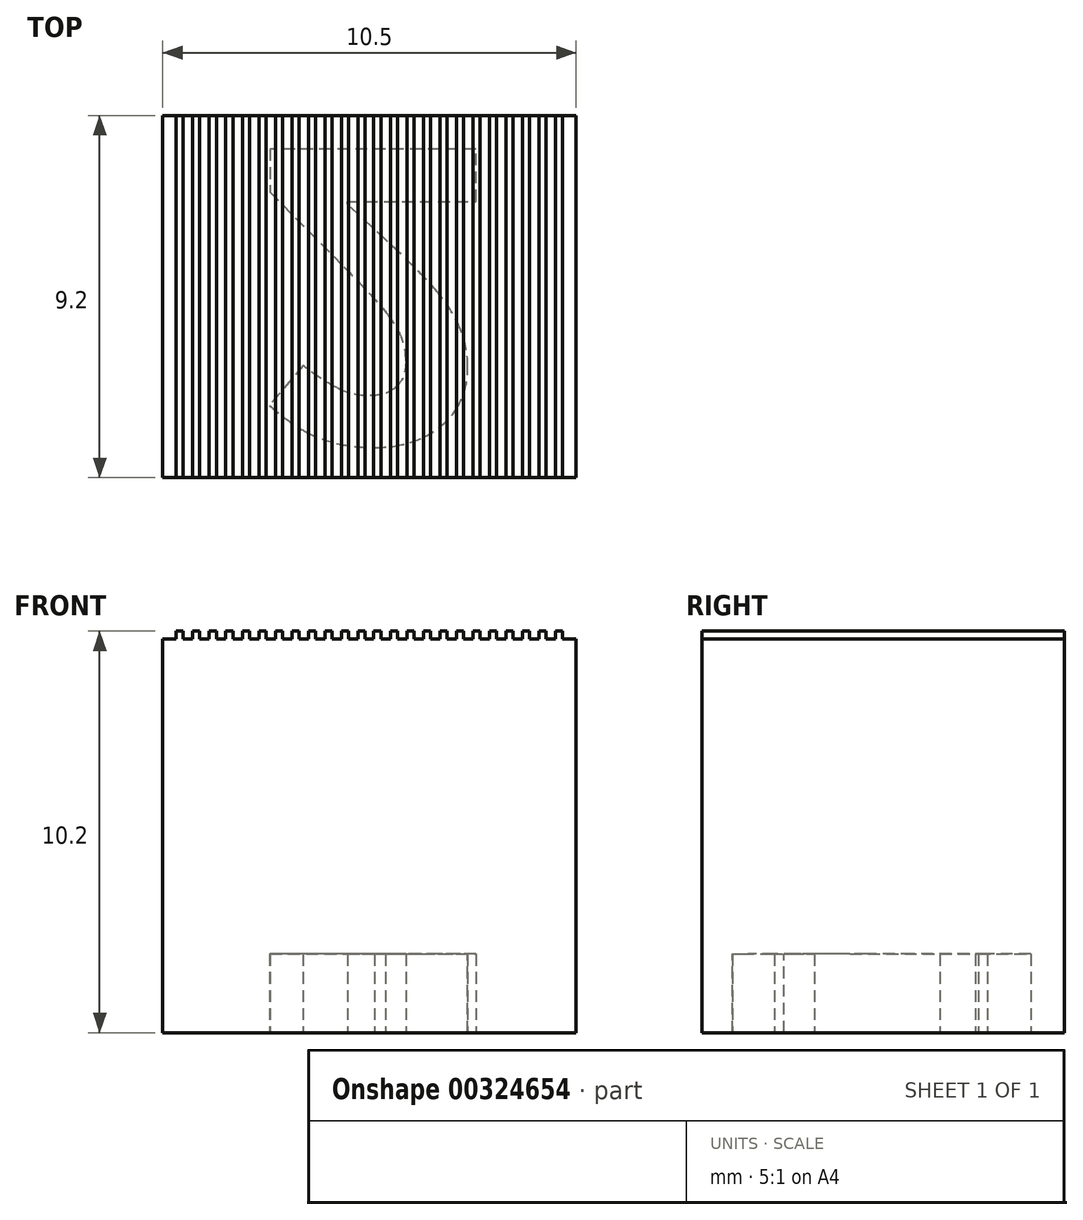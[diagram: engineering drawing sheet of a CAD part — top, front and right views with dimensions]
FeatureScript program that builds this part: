
annotation { "Feature Type Name" : "Feature", "Feature Type Description" : "" }
export const myFeature = defineFeature(function(context is Context, id is Id, definition is map)
    precondition{}
    {
        {
            assignVariable(context, id + "F0", {"name" : "h", "anyValue" : 10});
        }
        {
            assignVariable(context, id + "F1", {"name" : "gh", "anyValue" : 0.2});
        }
        {
            var Q0;
            Q0=qCreatedBy(makeId("Top.planeOp"),FACE);
            var sketch = newSketch(context, id + "F2", { "sketchPlane" : qUnion([Q0])});
            skLineSegment(sketch, "E0.bottom", {"start": v(5.25, 4.6) * mm, "end": v(-5.25, 4.6) * mm});
            skLineSegment(sketch, "E0.top", {"start": v(5.25, -4.6) * mm, "end": v(-5.25, -4.6) * mm});
            skLineSegment(sketch, "E0.left", {"start": v(5.25, 4.6) * mm, "end": v(5.25, -4.6) * mm});
            skLineSegment(sketch, "E0.right", {"start": v(-5.25, 4.6) * mm, "end": v(-5.25, -4.6) * mm});
            skPoint(sketch, "E0.middle", {"position": v(0, 0) * mm});
            skSolve(sketch);
        }
        {
            var Q0;
            Q0=qSketchRegion(id+"F2",true);
            extrude(context, id + "F3", {"entities" : qUnion([Q0]), "depth" : (getVariable(context, 'h')) * mm});
        }
        {
            var Q0;
            Q0=makeQuery(id+"F3.opExtrude","CAP_FACE",FACE,{"disambiguationData":[OSD([sQuery(id+"F2.wireOp",EDGE,"E0.bottom"),sQuery(id+"F2.wireOp",EDGE,"E0.top"),sQuery(id+"F2.wireOp",EDGE,"E0.left"),sQuery(id+"F2.wireOp",EDGE,"E0.right")])],"isStart":false});
            var sketch = newSketch(context, id + "F4", { "sketchPlane" : qUnion([Q0])});
            skLineSegment(sketch, "E1", {"start": v(0.1, 4.6) * mm, "end": v(0.11, -4.6) * mm});
            skLineSegment(sketch, "E2", {"start": v(-0.1, -4.6) * mm, "end": v(-0.11, 4.6) * mm, "construction": true});
            skLineSegment(sketch, "E3", {"start": v(0.3, -4.6) * mm, "end": v(0.29, 4.6) * mm});
            skLineSegment(sketch, "E4", {"start": v(0.1, 0) * mm, "end": v(-0.1, 0) * mm, "construction": true});
            skPoint(sketch, "E5", {"position": v(0, 0) * mm});
            skLineSegment(sketch, "E6", {"start": v(0.11, 4.6) * mm, "end": v(0.29, 4.6) * mm});
            skLineSegment(sketch, "E7", {"start": v(0.29, -4.6) * mm, "end": v(0.11, -4.6) * mm});
            skLineSegment(sketch, "E8.1.0.0", {"start": v(0.53, 4.6) * mm, "end": v(0.71, 4.6) * mm});
            skLineSegment(sketch, "E8.1.0.1", {"start": v(0.71, -4.6) * mm, "end": v(0.7, 4.6) * mm});
            skLineSegment(sketch, "E8.1.0.2", {"start": v(0.53, 4.6) * mm, "end": v(0.53, -4.6) * mm});
            skLineSegment(sketch, "E8.1.0.3", {"start": v(0.71, -4.6) * mm, "end": v(0.53, -4.6) * mm});
            skLineSegment(sketch, "E8.direction1", {"start": v(0.11, 4.6) * mm, "end": v(0.53, 4.6) * mm, "construction": true});
            skLineSegment(sketch, "E9.MirrorCS", {"start": v(-0.1, 0) * mm, "end": v(0.1, 0) * mm, "construction": true});
            skLineSegment(sketch, "E10.MirrorCS", {"start": v(-0.1, 4.6) * mm, "end": v(-0.1, -4.6) * mm});
            skLineSegment(sketch, "E11.MirrorCS", {"start": v(0.11, -4.6) * mm, "end": v(0.1, 4.6) * mm, "construction": true});
            skLineSegment(sketch, "E12.0.2.0", {"start": v(0.95, 4.6) * mm, "end": v(1.13, 4.6) * mm});
            skLineSegment(sketch, "E12.3.2.0", {"start": v(1.13, -4.6) * mm, "end": v(1.13, 4.6) * mm});
            skLineSegment(sketch, "E12.6.2.0", {"start": v(0.95, 4.6) * mm, "end": v(0.95, -4.6) * mm});
            skLineSegment(sketch, "E12.9.2.0", {"start": v(1.13, -4.6) * mm, "end": v(0.95, -4.6) * mm});
            skLineSegment(sketch, "E12.0.3.0", {"start": v(1.37, 4.6) * mm, "end": v(1.55, 4.6) * mm});
            skLineSegment(sketch, "E12.3.3.0", {"start": v(1.55, -4.6) * mm, "end": v(1.55, 4.6) * mm});
            skLineSegment(sketch, "E12.6.3.0", {"start": v(1.37, 4.6) * mm, "end": v(1.37, -4.6) * mm});
            skLineSegment(sketch, "E12.9.3.0", {"start": v(1.55, -4.6) * mm, "end": v(1.37, -4.6) * mm});
            skLineSegment(sketch, "E12.0.4.0", {"start": v(1.79, 4.6) * mm, "end": v(1.97, 4.6) * mm});
            skLineSegment(sketch, "E12.3.4.0", {"start": v(1.97, -4.6) * mm, "end": v(1.97, 4.6) * mm});
            skLineSegment(sketch, "E12.6.4.0", {"start": v(1.79, 4.6) * mm, "end": v(1.79, -4.6) * mm});
            skLineSegment(sketch, "E12.9.4.0", {"start": v(1.97, -4.6) * mm, "end": v(1.79, -4.6) * mm});
            skLineSegment(sketch, "E13.0.5.0", {"start": v(2.2, 4.6) * mm, "end": v(2.39, 4.6) * mm});
            skLineSegment(sketch, "E13.3.5.0", {"start": v(2.39, -4.6) * mm, "end": v(2.39, 4.6) * mm});
            skLineSegment(sketch, "E13.6.5.0", {"start": v(2.2, 4.6) * mm, "end": v(2.2, -4.6) * mm});
            skLineSegment(sketch, "E13.9.5.0", {"start": v(2.39, -4.6) * mm, "end": v(2.2, -4.6) * mm});
            skLineSegment(sketch, "E14.0.6.0", {"start": v(2.63, 4.6) * mm, "end": v(2.8, 4.6) * mm});
            skLineSegment(sketch, "E14.3.6.0", {"start": v(2.8, -4.6) * mm, "end": v(2.8, 4.6) * mm});
            skLineSegment(sketch, "E14.6.6.0", {"start": v(2.63, 4.6) * mm, "end": v(2.63, -4.6) * mm});
            skLineSegment(sketch, "E14.9.6.0", {"start": v(2.8, -4.6) * mm, "end": v(2.63, -4.6) * mm});
            skLineSegment(sketch, "E14.0.7.0", {"start": v(3.05, 4.6) * mm, "end": v(3.23, 4.6) * mm});
            skLineSegment(sketch, "E14.3.7.0", {"start": v(3.23, -4.6) * mm, "end": v(3.23, 4.6) * mm});
            skLineSegment(sketch, "E14.6.7.0", {"start": v(3.05, 4.6) * mm, "end": v(3.05, -4.6) * mm});
            skLineSegment(sketch, "E14.9.7.0", {"start": v(3.23, -4.6) * mm, "end": v(3.05, -4.6) * mm});
            skLineSegment(sketch, "E14.0.8.0", {"start": v(3.47, 4.6) * mm, "end": v(3.65, 4.6) * mm});
            skLineSegment(sketch, "E14.3.8.0", {"start": v(3.65, -4.6) * mm, "end": v(3.65, 4.6) * mm});
            skLineSegment(sketch, "E14.6.8.0", {"start": v(3.47, 4.6) * mm, "end": v(3.47, -4.6) * mm});
            skLineSegment(sketch, "E14.9.8.0", {"start": v(3.65, -4.6) * mm, "end": v(3.47, -4.6) * mm});
            skLineSegment(sketch, "E14.0.9.0", {"start": v(3.89, 4.6) * mm, "end": v(4.07, 4.6) * mm});
            skLineSegment(sketch, "E14.3.9.0", {"start": v(4.07, -4.6) * mm, "end": v(4.07, 4.6) * mm});
            skLineSegment(sketch, "E14.6.9.0", {"start": v(3.89, 4.6) * mm, "end": v(3.89, -4.6) * mm});
            skLineSegment(sketch, "E14.9.9.0", {"start": v(4.07, -4.6) * mm, "end": v(3.89, -4.6) * mm});
            skLineSegment(sketch, "E14.0.10.0", {"start": v(4.3, 4.6) * mm, "end": v(4.49, 4.6) * mm});
            skLineSegment(sketch, "E14.3.10.0", {"start": v(4.49, -4.6) * mm, "end": v(4.49, 4.6) * mm});
            skLineSegment(sketch, "E14.6.10.0", {"start": v(4.3, 4.6) * mm, "end": v(4.3, -4.6) * mm});
            skLineSegment(sketch, "E14.9.10.0", {"start": v(4.49, -4.6) * mm, "end": v(4.3, -4.6) * mm});
            skLineSegment(sketch, "E14.0.11.0", {"start": v(4.73, 4.6) * mm, "end": v(4.9, 4.6) * mm});
            skLineSegment(sketch, "E14.3.11.0", {"start": v(4.9, -4.6) * mm, "end": v(4.9, 4.6) * mm});
            skLineSegment(sketch, "E14.6.11.0", {"start": v(4.73, 4.6) * mm, "end": v(4.73, -4.6) * mm});
            skLineSegment(sketch, "E14.9.11.0", {"start": v(4.9, -4.6) * mm, "end": v(4.73, -4.6) * mm});
            skLineSegment(sketch, "E15.MirrorCS", {"start": v(-0.11, 4.6) * mm, "end": v(-0.29, 4.6) * mm});
            skLineSegment(sketch, "E16.MirrorCS", {"start": v(-4.73, 4.6) * mm, "end": v(-4.9, 4.6) * mm});
            skLineSegment(sketch, "E17.MirrorCS", {"start": v(-3.89, 4.6) * mm, "end": v(-4.07, 4.6) * mm});
            skLineSegment(sketch, "E18.MirrorCS", {"start": v(-4.3, 4.6) * mm, "end": v(-4.49, 4.6) * mm});
            skLineSegment(sketch, "E19.MirrorCS", {"start": v(-0.11, 4.6) * mm, "end": v(-0.53, 4.6) * mm, "construction": true});
            skLineSegment(sketch, "E20.MirrorCS", {"start": v(-2.63, 4.6) * mm, "end": v(-2.8, 4.6) * mm});
            skLineSegment(sketch, "E21.MirrorCS", {"start": v(-1.79, 4.6) * mm, "end": v(-1.97, 4.6) * mm});
            skLineSegment(sketch, "E22.MirrorCS", {"start": v(-2.2, 4.6) * mm, "end": v(-2.39, 4.6) * mm});
            skLineSegment(sketch, "E23.MirrorCS", {"start": v(-0.95, 4.6) * mm, "end": v(-1.13, 4.6) * mm});
            skLineSegment(sketch, "E24.MirrorCS", {"start": v(-3.47, 4.6) * mm, "end": v(-3.65, 4.6) * mm});
            skLineSegment(sketch, "E25.MirrorCS", {"start": v(-0.53, 4.6) * mm, "end": v(-0.71, 4.6) * mm});
            skLineSegment(sketch, "E26.MirrorCS", {"start": v(-3.05, 4.6) * mm, "end": v(-3.23, 4.6) * mm});
            skLineSegment(sketch, "E27.MirrorCS", {"start": v(-1.37, 4.6) * mm, "end": v(-1.55, 4.6) * mm});
            skLineSegment(sketch, "E28.MirrorCS", {"start": v(-0.3, -4.6) * mm, "end": v(-0.29, 4.6) * mm});
            skLineSegment(sketch, "E29.MirrorCS", {"start": v(-0.53, 4.6) * mm, "end": v(-0.53, -4.6) * mm});
            skLineSegment(sketch, "E30.MirrorCS", {"start": v(-0.71, -4.6) * mm, "end": v(-0.7, 4.6) * mm});
            skLineSegment(sketch, "E31.MirrorCS", {"start": v(-0.95, 4.6) * mm, "end": v(-0.95, -4.6) * mm});
            skLineSegment(sketch, "E32.MirrorCS", {"start": v(-1.13, -4.6) * mm, "end": v(-1.13, 4.6) * mm});
            skLineSegment(sketch, "E33.MirrorCS", {"start": v(-1.37, 4.6) * mm, "end": v(-1.37, -4.6) * mm});
            skLineSegment(sketch, "E34.MirrorCS", {"start": v(-1.55, -4.6) * mm, "end": v(-1.55, 4.6) * mm});
            skLineSegment(sketch, "E35.MirrorCS", {"start": v(-1.79, 4.6) * mm, "end": v(-1.79, -4.6) * mm});
            skLineSegment(sketch, "E36.MirrorCS", {"start": v(-1.97, -4.6) * mm, "end": v(-1.97, 4.6) * mm});
            skLineSegment(sketch, "E37.MirrorCS", {"start": v(-2.2, 4.6) * mm, "end": v(-2.2, -4.6) * mm});
            skLineSegment(sketch, "E38.MirrorCS", {"start": v(-2.39, -4.6) * mm, "end": v(-2.39, 4.6) * mm});
            skLineSegment(sketch, "E39.MirrorCS", {"start": v(-2.63, 4.6) * mm, "end": v(-2.63, -4.6) * mm});
            skLineSegment(sketch, "E40.MirrorCS", {"start": v(-2.8, -4.6) * mm, "end": v(-2.8, 4.6) * mm});
            skLineSegment(sketch, "E41.MirrorCS", {"start": v(-3.05, 4.6) * mm, "end": v(-3.05, -4.6) * mm});
            skLineSegment(sketch, "E42.MirrorCS", {"start": v(-3.23, -4.6) * mm, "end": v(-3.23, 4.6) * mm});
            skLineSegment(sketch, "E43.MirrorCS", {"start": v(-3.47, 4.6) * mm, "end": v(-3.47, -4.6) * mm});
            skLineSegment(sketch, "E44.MirrorCS", {"start": v(-3.65, -4.6) * mm, "end": v(-3.65, 4.6) * mm});
            skLineSegment(sketch, "E45.MirrorCS", {"start": v(-3.89, 4.6) * mm, "end": v(-3.89, -4.6) * mm});
            skLineSegment(sketch, "E46.MirrorCS", {"start": v(-4.07, -4.6) * mm, "end": v(-4.07, 4.6) * mm});
            skLineSegment(sketch, "E47.MirrorCS", {"start": v(-4.3, 4.6) * mm, "end": v(-4.3, -4.6) * mm});
            skLineSegment(sketch, "E48.MirrorCS", {"start": v(-4.49, -4.6) * mm, "end": v(-4.49, 4.6) * mm});
            skLineSegment(sketch, "E49.MirrorCS", {"start": v(-4.73, 4.6) * mm, "end": v(-4.73, -4.6) * mm});
            skLineSegment(sketch, "E50.MirrorCS", {"start": v(-4.9, -4.6) * mm, "end": v(-4.9, 4.6) * mm});
            skLineSegment(sketch, "E51.MirrorCS", {"start": v(-0.29, -4.6) * mm, "end": v(-0.11, -4.6) * mm});
            skLineSegment(sketch, "E52.MirrorCS", {"start": v(-1.13, -4.6) * mm, "end": v(-0.95, -4.6) * mm});
            skLineSegment(sketch, "E53.MirrorCS", {"start": v(-2.8, -4.6) * mm, "end": v(-2.63, -4.6) * mm});
            skLineSegment(sketch, "E54.MirrorCS", {"start": v(-1.55, -4.6) * mm, "end": v(-1.37, -4.6) * mm});
            skLineSegment(sketch, "E55.MirrorCS", {"start": v(-3.65, -4.6) * mm, "end": v(-3.47, -4.6) * mm});
            skLineSegment(sketch, "E56.MirrorCS", {"start": v(-3.23, -4.6) * mm, "end": v(-3.05, -4.6) * mm});
            skLineSegment(sketch, "E57.MirrorCS", {"start": v(-4.49, -4.6) * mm, "end": v(-4.3, -4.6) * mm});
            skLineSegment(sketch, "E58.MirrorCS", {"start": v(-0.71, -4.6) * mm, "end": v(-0.53, -4.6) * mm});
            skLineSegment(sketch, "E59.MirrorCS", {"start": v(-4.9, -4.6) * mm, "end": v(-4.73, -4.6) * mm});
            skLineSegment(sketch, "E60.MirrorCS", {"start": v(-2.39, -4.6) * mm, "end": v(-2.2, -4.6) * mm});
            skLineSegment(sketch, "E61.MirrorCS", {"start": v(-4.07, -4.6) * mm, "end": v(-3.89, -4.6) * mm});
            skLineSegment(sketch, "E62.MirrorCS", {"start": v(-1.97, -4.6) * mm, "end": v(-1.79, -4.6) * mm});
            skSolve(sketch);
        }
        {
            var Q0;
            Q0=qSketchRegion(id+"F4",true);
            extrude(context, id + "F5", {"entities" : qUnion([Q0]), "operationType" : NewBodyOperationType.ADD, "depth" : (getVariable(context, 'gh')) * mm});
        }
        {
            var Q0;
            Q0 = qSketchRegion(id + "F4", true);
            extrude(context, id + "F6", {"entities" : qUnion([Q0]), "operationType" : NewBodyOperationType.ADD, "depth" : (getVariable(context, 'gh')) * mm});
        }
        {
            var Q0;
            Q0=makeQuery(id+"F3.opExtrude","CAP_FACE",FACE,{"disambiguationData":[OSD([sQuery(id+"F2.wireOp",EDGE,"E0.bottom"),sQuery(id+"F2.wireOp",EDGE,"E0.top"),sQuery(id+"F2.wireOp",EDGE,"E0.left"),sQuery(id+"F2.wireOp",EDGE,"E0.right")])],"isStart":true});
            var sketch = newSketch(context, id + "F7", { "sketchPlane" : qUnion([Q0])});
            skText(sketch, "E63", { "text": "2", "fontName": "OpenSans-Bold.ttf"});
            const initialGuessF7  = {"E63": [-0.00294, -0.00375, 1, 0, 0.00754]};
            skSetInitialGuess(sketch, initialGuessF7);
            skSolve(sketch);
        }
        {
            var Q0;
            Q0 = qSketchRegion(id + "F7", true);
            extrude(context, id + "F8", {"entities" : qUnion([Q0]), "operationType" : NewBodyOperationType.REMOVE, "oppositeDirection" : true, "depth" : 2 * mm});
        }
    });
